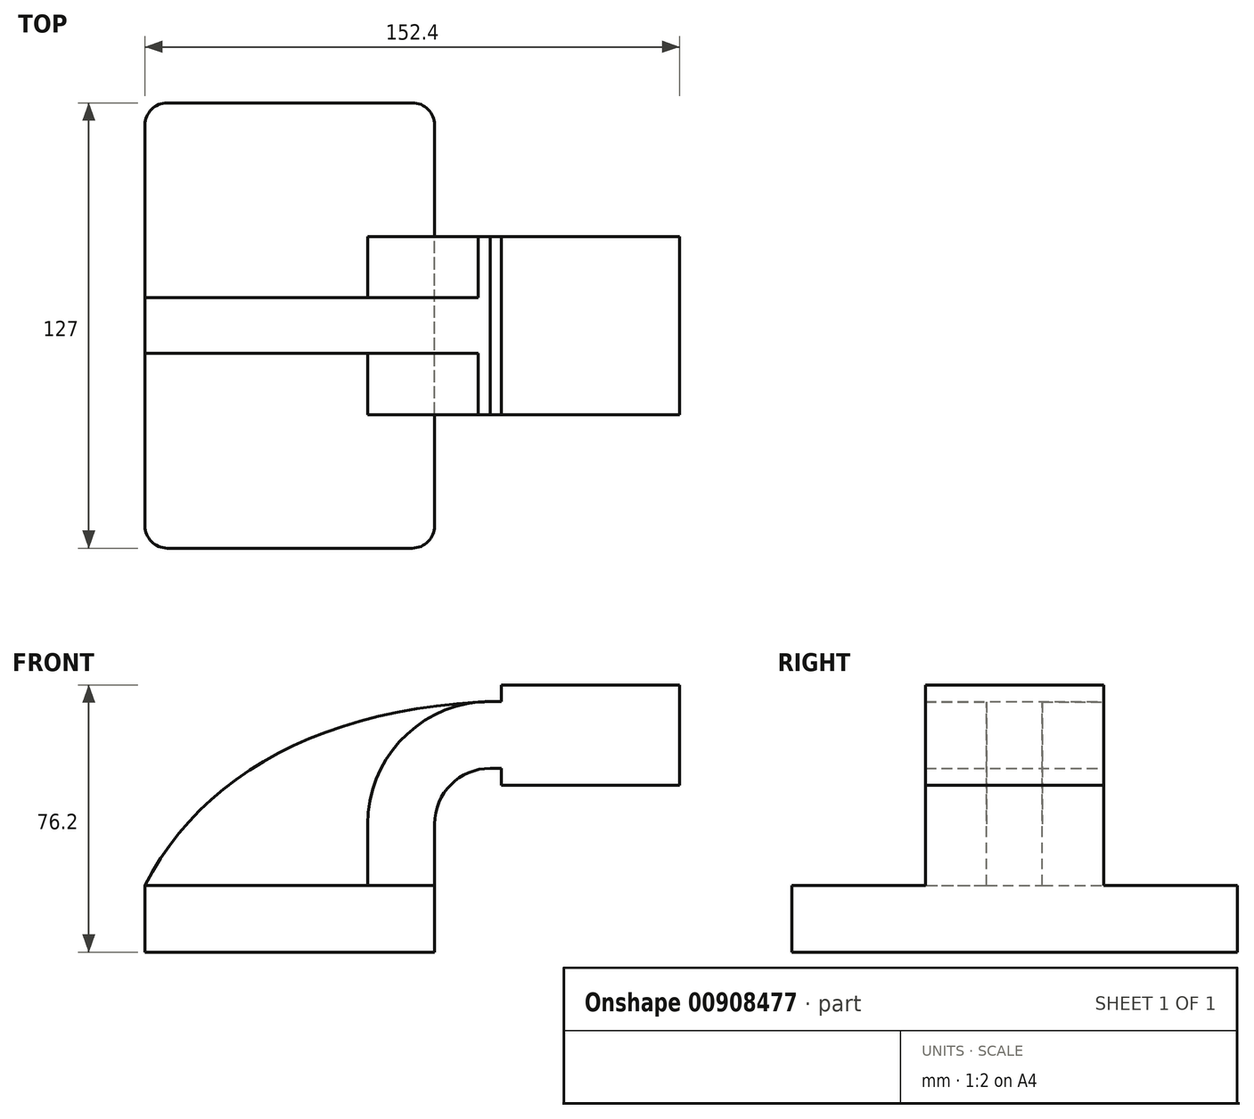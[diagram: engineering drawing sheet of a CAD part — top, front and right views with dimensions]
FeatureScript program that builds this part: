
annotation { "Feature Type Name" : "Feature", "Feature Type Description" : "" }
export const myFeature = defineFeature(function(context is Context, id is Id, definition is map)
    precondition{}
    {
        {
            var Q0;
            Q0=qCreatedBy(makeId("Front.planeOp"),FACE);
            var sketch = newSketch(context, id + "F0", { "sketchPlane" : qUnion([Q0])});
            skLineSegment(sketch, "E0.bottom", {"start": v(-41.28, 9.52) * mm, "end": v(41.28, 9.53) * mm});
            skLineSegment(sketch, "E0.top", {"start": v(-41.28, -9.53) * mm, "end": v(41.28, -9.53) * mm});
            skLineSegment(sketch, "E0.left", {"start": v(-41.28, 9.52) * mm, "end": v(-41.28, -9.53) * mm});
            skLineSegment(sketch, "E0.right", {"start": v(41.28, 9.53) * mm, "end": v(41.28, -9.52) * mm});
            skPoint(sketch, "E0.middle", {"position": v(0, 0) * mm});
            skLineSegment(sketch, "E1.bottom", {"start": v(60.33, 38.1) * mm, "end": v(111.12, 38.1) * mm});
            skLineSegment(sketch, "E1.top", {"start": v(60.33, 66.67) * mm, "end": v(111.12, 66.67) * mm});
            skLineSegment(sketch, "E1.left", {"start": v(60.33, 38.1) * mm, "end": v(60.33, 66.68) * mm});
            skLineSegment(sketch, "E1.right", {"start": v(111.12, 38.1) * mm, "end": v(111.12, 66.68) * mm});
            skPoint(sketch, "E1.middle", {"position": v(85.73, 52.39) * mm});
            skLineSegment(sketch, "E2", {"start": v(41.27, 9.53) * mm, "end": v(41.27, 27) * mm});
            skArc(sketch, "E3", {"start": v(41.27, 27) * mm, "mid": v(45.92, 38.23) * mm, "end": v(57.15, 42.88) * mm});
            skLineSegment(sketch, "E4", {"start": v(57.15, 42.88) * mm, "end": v(82.9, 42.88) * mm});
            skLineSegment(sketch, "E5.0", {"start": v(57.15, 61.93) * mm, "end": v(82.9, 61.93) * mm});
            skArc(sketch, "E5.1", {"start": v(22.23, 27) * mm, "mid": v(32.45, 51.7) * mm, "end": v(57.15, 61.93) * mm});
            skLineSegment(sketch, "E5.2", {"start": v(22.22, 9.53) * mm, "end": v(22.22, 27) * mm});
            skLineSegment(sketch, "E6", {"start": v(85.72, 66.67) * mm, "end": v(85.73, 38.1) * mm});
            skLineSegment(sketch, "E7.0", {"start": v(57.15, 55.58) * mm, "end": v(82.9, 55.58) * mm});
            skFitSpline(sketch, "E8", {"points": [v(-41.28, 9.52) * mm, v(57.15, 61.93) * mm], "startDerivative": vector(48.06, 93.17) * mm, "endDerivative": vector(145.69, 5.82) * mm});
            skSolve(sketch);
        }
        {
            var Q0;
            Q0=makeQuery(id+"F0.imprint","IMPRINT",FACE,{"disambiguationData":[TD([[makeQuery(id+"F0.imprint","IMPRINT",EDGE,{"derivedFrom":sQuery(id+"F0.wireOp",EDGE,"E0.top")}),1.0]])]});
            extrude(context, id + "F1", {"entities" : qUnion([Q0]), "endBound" : BoundingType.SYMMETRIC, "depth" : 127 * mm, "offsetDistance" : 25.4 * mm});
        }
        {
            var Q0;
            {var subQ0=sQuery(id+"F0.wireOp",EDGE,"E2");Q0=makeQuery(id+"F0.imprint","IMPRINT",FACE,{"disambiguationData":[TD([[makeQuery(id+"F0.imprint","IMPRINT",EDGE,{"derivedFrom":subQ0}),1.0]])]});}
            var Q1;
            {var subQ6=sQuery(id+"F0.wireOp",EDGE,"E6");Q1=makeQuery(id+"F0.imprint","IMPRINT",FACE,{"disambiguationData":[TD([[makeQuery(id+"F0.imprint","IMPRINT",EDGE,{"derivedFrom":subQ6}),-1.0]])]});}
            var Q2;
            {var subQ0=sQuery(id+"F0.wireOp",EDGE,"E1.right");Q2=makeQuery(id+"F0.imprint","IMPRINT",FACE,{"disambiguationData":[TD([[makeQuery(id+"F0.imprint","IMPRINT",EDGE,{"derivedFrom":subQ0}),1.0]])]});}
            extrude(context, id + "F2", {"entities" : qUnion([Q0, Q1, Q2]), "operationType" : NewBodyOperationType.ADD, "endBound" : BoundingType.SYMMETRIC, "depth" : 50.8 * mm, "offsetDistance" : 25.4 * mm});
        }
        {
            var Q0;
            {var subQ3=sQuery(id+"F0.wireOp",EDGE,"E5.2");Q0=makeQuery(id+"F0.imprint","IMPRINT",FACE,{"disambiguationData":[TD([[makeQuery(id+"F0.imprint","IMPRINT",EDGE,{"derivedFrom":subQ3}),1.0]])]});}
            extrude(context, id + "F3", {"entities" : qUnion([Q0]), "operationType" : NewBodyOperationType.ADD, "endBound" : BoundingType.SYMMETRIC, "depth" : 15.88 * mm, "offsetDistance" : 25.4 * mm});
        }
        {
            var Q0;
            {var subQ0=sQuery(id+"F0.wireOp",EDGE,"E1.right");Q0=makeQuery(id+"F0.imprint","IMPRINT",FACE,{"disambiguationData":[TD([[makeQuery(id+"F0.imprint","IMPRINT",EDGE,{"derivedFrom":subQ0}),1.0]])]});}
            var Q1;
            Q1=sQuery(id+"F0.wireOp",EDGE,"E6");
            revolve(context, id + "F4", {"operationType" : NewBodyOperationType.ADD, "surfaceOperationType" : NewSurfaceOperationType.NEW, "entities" : qUnion([Q0]), "axis" : qUnion([Q1]), "revolveType" : RevolveType.FULL});
        }
        {
            var Q0;
            Q0=makeQuery(id+"F1.opExtrude","CAP_EDGE",EDGE,{"disambiguationData":[OSD([sQuery(id+"F0.wireOp",EDGE,"E0.right")])],"isStart":false});
            var Q1;
            Q1=makeQuery(id+"F1.opExtrude","CAP_EDGE",EDGE,{"disambiguationData":[OSD([sQuery(id+"F0.wireOp",EDGE,"E0.right")])],"isStart":true});
            var Q2;
            Q2=makeQuery(id+"F1.opExtrude","CAP_EDGE",EDGE,{"disambiguationData":[OSD([sQuery(id+"F0.wireOp",EDGE,"E0.left")])],"isStart":false});
            var Q3;
            Q3=makeQuery(id+"F1.opExtrude","CAP_EDGE",EDGE,{"disambiguationData":[OSD([sQuery(id+"F0.wireOp",EDGE,"E0.left")])],"isStart":true});
            fillet(context, id + "F5", {"entities" : qUnion([Q0, Q1, Q2, Q3]), "radius" : 6.35 * mm, "tangentPropagation" : true, "allowEdgeOverflow" : false});
        }
    });
